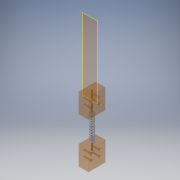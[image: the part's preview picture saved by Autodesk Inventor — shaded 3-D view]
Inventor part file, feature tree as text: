
AUTODESK INVENTOR PART (.ipt)
format: ipt  version: 2016 (Build 200138000, 138)  size: 458,240 bytes
history: native  units: in
note: dims shown in document units (in); Inventor stores cm internally (conversion verified against a paired STEP export)
features: reference x2, surface_op x2, other x2, plane x1, helix x1, sketch x1
ambient origin geometry x8: Origin, YZ Plane, XZ Plane, XY Plane, X Axis, Y Axis, Z Axis, Center Point
bodies: Solid1 (feature_tree)
feature tree (9):
  plane  "Work Plane1"
  helix  "Coil1"  [1 undecoded]
  sketch  "Sketch1"  dims[d1=0.195in d2=2.63in d3=1.0in d4=2.63in d5=7.4803in d6=0.0in d7=90.0deg d8=90.0deg d9=0.0in d10=0.0in]
  reference  "Reference1"
  reference  "Reference2"
  surface_op  "Surface1"
  surface_op  "Surface2"
  other  "Srf1"
  other  "Srf2"
note: 1 required parameter value undecoded (feature->parameter linkage not recoverable at this tier; creation-order binding heuristic only, values carry confidence <= 0.55)
